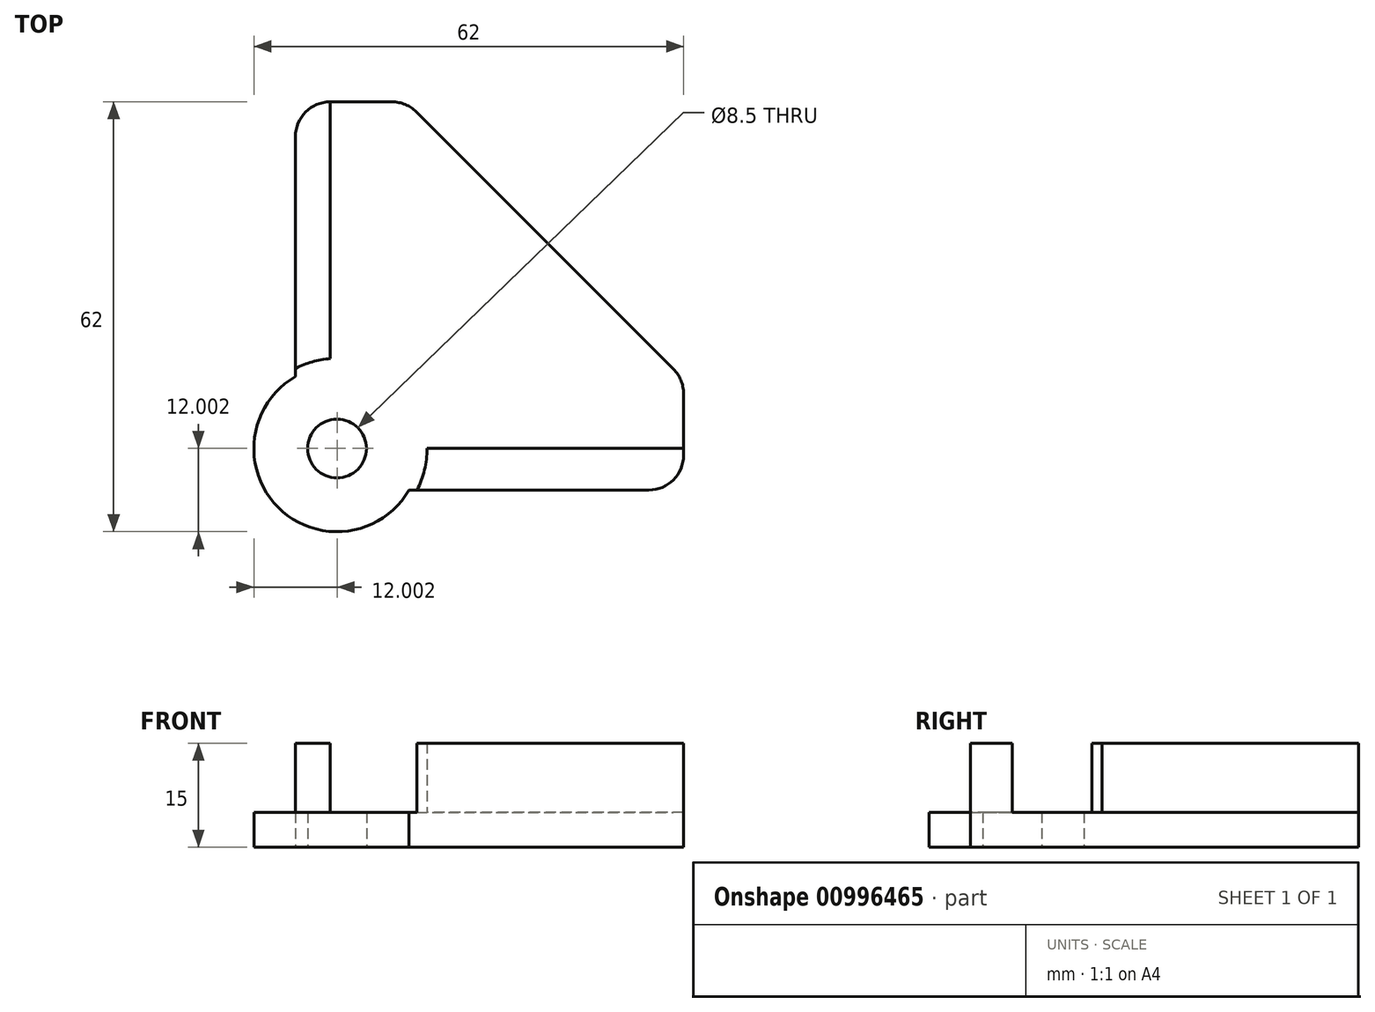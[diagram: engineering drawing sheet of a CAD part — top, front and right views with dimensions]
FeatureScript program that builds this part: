
annotation { "Feature Type Name" : "Feature", "Feature Type Description" : "" }
export const myFeature = defineFeature(function(context is Context, id is Id, definition is map)
    precondition{}
    {
        {
            var Q0;
            Q0=qCreatedBy(makeId("Top.planeOp"),FACE);
            var sketch = newSketch(context, id + "F0", { "sketchPlane" : qUnion([Q0])});
            skSolve(sketch);
        }
        {
            var Q0;
            Q0=qCreatedBy(makeId("Top.planeOp"),FACE);
            var sketch = newSketch(context, id + "F1", { "sketchPlane" : qUnion([Q0])});
            skLineSegment(sketch, "E0", {"start": v(-0.62, 0.86) * mm, "end": v(39.38, 0.86) * mm});
            skLineSegment(sketch, "E1", {"start": v(39.38, 0.86) * mm, "end": v(39.38, -9.14) * mm});
            skLineSegment(sketch, "E2", {"start": v(39.38, -9.14) * mm, "end": v(2.38, -9.14) * mm});
            skLineSegment(sketch, "E3", {"start": v(-0.62, 40.86) * mm, "end": v(-0.62, 0.86) * mm});
            skArc(sketch, "E4", {"start": v(-16.62, 1.25) * mm, "mid": v(-19.1, -17.62) * mm, "end": v(-0.23, -15.14) * mm});
            skLineSegment(sketch, "E5", {"start": v(-16.62, 40.86) * mm, "end": v(-0.62, 40.86) * mm});
            skLineSegment(sketch, "E6", {"start": v(39.38, -9.14) * mm, "end": v(39.38, -9.14) * mm});
            skLineSegment(sketch, "E7", {"start": v(39.38, -15.14) * mm, "end": v(39.38, -9.14) * mm});
            skCircle(sketch, "E8", {"center": v(-10.62, -9.14) * mm, "radius": 4.25 * mm});
            skLineSegment(sketch, "E9", {"start": v(-0.62, 40.86) * mm, "end": v(39.38, 0.86) * mm});
            skLineSegment(sketch, "E10", {"start": v(-16.62, 40.86) * mm, "end": v(-16.62, 1.25) * mm});
            skLineSegment(sketch, "E11", {"start": v(39.38, -15.14) * mm, "end": v(-0.23, -15.14) * mm});
            skPoint(sketch, "E12.start.orphan", {"position": v(-22.62, -9.14) * mm});
            skArc(sketch, "E13", {"start": v(-11.62, 3.82) * mm, "mid": v(-14.2, 3.36) * mm, "end": v(-16.62, 2.4) * mm});
            skArc(sketch, "E14.trimOffspring", {"start": v(0.91, -15.14) * mm, "mid": v(2, -12.23) * mm, "end": v(2.38, -9.14) * mm});
            skLineSegment(sketch, "E15", {"start": v(-11.62, 40.86) * mm, "end": v(-11.62, 3.82) * mm});
            skSolve(sketch);
        }
        {
            var Q0;
            Q0=makeQuery(id+"F1.imprint","IMPRINT",FACE,{"disambiguationData":[TD([[makeQuery(id+"F1.imprint","IMPRINT",EDGE,{"derivedFrom":sQuery(id+"F1.wireOp",EDGE,"E0")}),-1.0]])]});
            var Q1;
            Q1=makeQuery(id+"F1.imprint","IMPRINT",FACE,{"disambiguationData":[TD([[makeQuery(id+"F1.imprint","IMPRINT",EDGE,{"derivedFrom":sQuery(id+"F1.wireOp",EDGE,"E0")}),1.0]])]});
            extrude(context, id + "F2", {"entities" : qUnion([Q0, Q1]), "depth" : 5 * mm, "offsetDistance" : 25 * mm});
        }
        {
            var Q0;
            Q0 = qSketchRegion(id + "F0", true);
            var Q1;
            {var subQ0=sQuery(id+"F1.wireOp",EDGE,"d625d911-7bf3-448f-b984-43d05a62372d");Q1=makeQuery(id+"F1.imprint","IMPRINT",FACE,{"disambiguationData":[TD([[makeQuery(id+"F1.imprint","IMPRINT",EDGE,{"derivedFrom":subQ0}),1.0]])]});}
            var Q2;
            {var subQ0=sQuery(id+"F1.wireOp",EDGE,"E2");Q2=makeQuery(id+"F1.imprint","IMPRINT",FACE,{"disambiguationData":[TD([[makeQuery(id+"F1.imprint","IMPRINT",EDGE,{"derivedFrom":subQ0}),1.0]])]});}
            var Q3;
            {var subQ4=sQuery(id+"F1.wireOp",EDGE,"E13");Q3=makeQuery(id+"F1.imprint","IMPRINT",FACE,{"disambiguationData":[TD([[makeQuery(id+"F1.imprint","IMPRINT",EDGE,{"derivedFrom":subQ4}),-1.0]])]});}
            extrude(context, id + "F3", {"entities" : qUnion([Q0, Q1, Q2, Q3]), "operationType" : NewBodyOperationType.ADD, "depth" : 15 * mm, "offsetDistance" : 25 * mm});
        }
        {
            var Q0;
            Q0=makeQuery(id+"F3.opExtrude","SWEPT_EDGE",EDGE,{"disambiguationData":[OSD([sQuery(id+"F1.wireOp",EDGE,"E7"),sQuery(id+"F1.wireOp",EDGE,"E11")])]});
            var Q1;
            Q1=makeQuery(id+"F3.opExtrude","SWEPT_EDGE",EDGE,{"disambiguationData":[OSD([sQuery(id+"F1.wireOp",EDGE,"E5"),sQuery(id+"F1.wireOp",EDGE,"E10")])]});
            var Q2;
            Q2=makeQuery(id+"F2.opExtrude","SWEPT_EDGE",EDGE,{"disambiguationData":[OSD([sQuery(id+"F1.wireOp",EDGE,"E0"),sQuery(id+"F1.wireOp",EDGE,"E1"),sQuery(id+"F1.wireOp",EDGE,"E9")])]});
            var Q3;
            Q3=makeQuery(id+"F2.opExtrude","SWEPT_EDGE",EDGE,{"disambiguationData":[OSD([sQuery(id+"F1.wireOp",EDGE,"4b9d8bef-c2e7-4a18-83fa-f95368f241aa"),sQuery(id+"F1.wireOp",EDGE,"E3"),sQuery(id+"F1.wireOp",EDGE,"E9")])]});
            fillet(context, id + "F4", {"entities" : qUnion([Q0, Q1, Q2, Q3]), "radius" : 5 * mm, "tangentPropagation" : true, "allowEdgeOverflow" : false});
        }
    });
